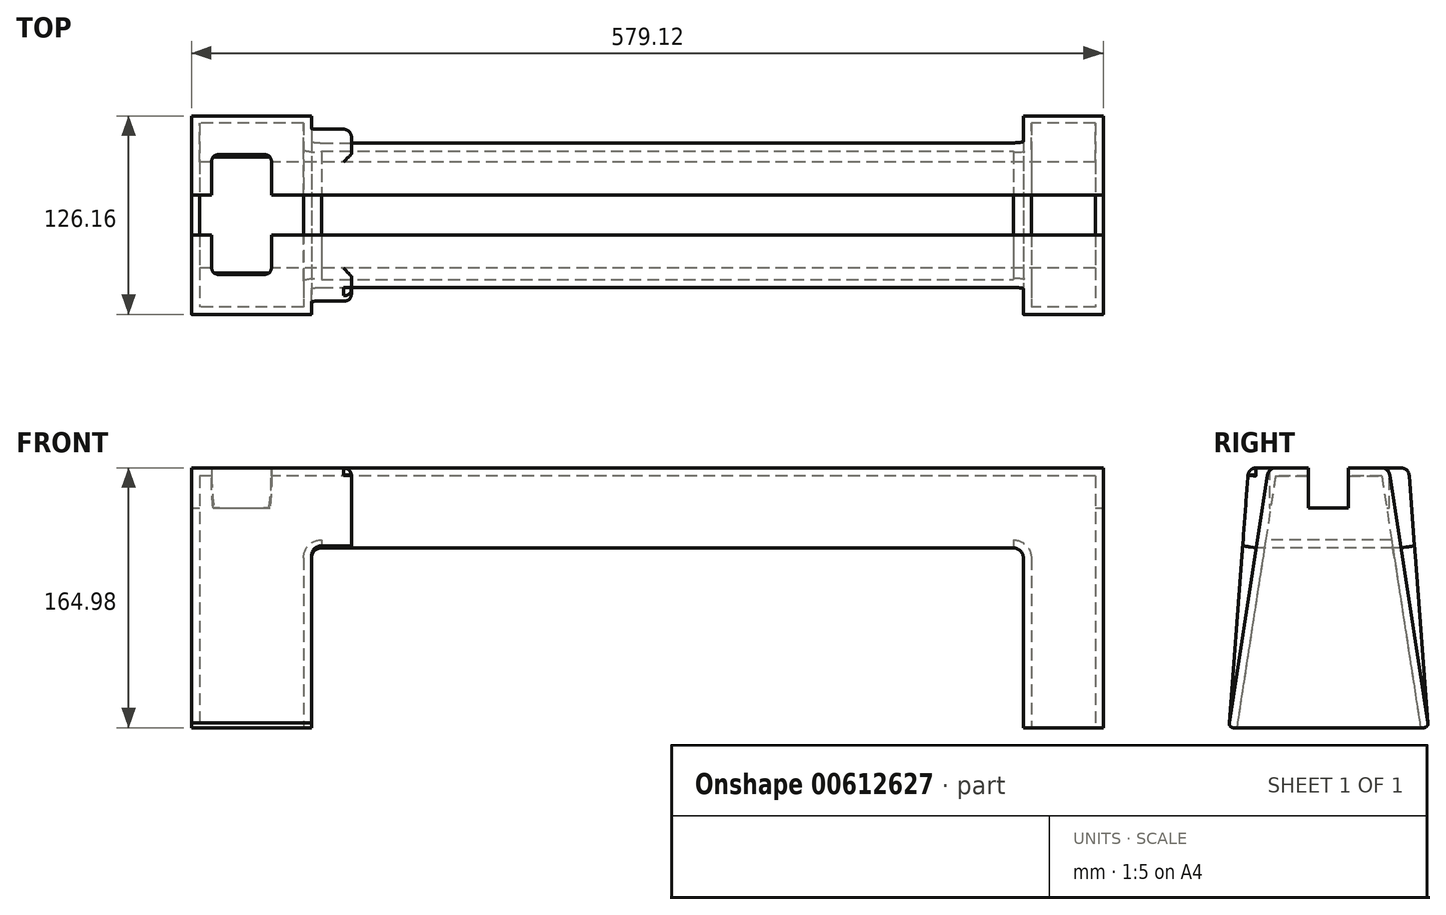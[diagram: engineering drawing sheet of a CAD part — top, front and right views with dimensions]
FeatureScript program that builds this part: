
annotation { "Feature Type Name" : "Feature", "Feature Type Description" : "" }
export const myFeature = defineFeature(function(context is Context, id is Id, definition is map)
    precondition{}
    {
        {
            var Q0;
            Q0=qCreatedBy(makeId("Right.planeOp"),FACE);
            var sketch = newSketch(context, id + "F0", { "sketchPlane" : qUnion([Q0])});
            skLineSegment(sketch, "E0.bottom", {"start": v(60.54, -82.5) * mm, "end": v(-60.54, -82.5) * mm});
            skLineSegment(sketch, "E0.top", {"start": v(38.1, 82.5) * mm, "end": v(-38.1, 82.5) * mm});
            skPoint(sketch, "E0.middle", {"position": v(0, 0) * mm});
            skPoint(sketch, "E1", {"position": v(0, 82.5) * mm});
            skPoint(sketch, "E2", {"position": v(-38.1, 82.5) * mm});
            skPoint(sketch, "E3", {"position": v(38.1, 82.5) * mm});
            skLineSegment(sketch, "E4", {"start": v(-38.1, 82.5) * mm, "end": v(-63.05, -79.57) * mm});
            skLineSegment(sketch, "E5", {"start": v(38.1, 82.5) * mm, "end": v(63.05, -79.57) * mm});
            skPoint(sketch, "E0.right.end.orphan", {"position": v(-63.5, 82.5) * mm});
            skPoint(sketch, "E0.left.end.orphan", {"position": v(63.5, 82.5) * mm});
            skLineSegment(sketch, "E6.filletArc", {"start": v(38.1, 82.5) * mm, "end": v(38.1, 82.5) * mm});
            skPoint(sketch, "E7.visualSharp", {"position": v(63.5, -82.5) * mm});
            skArc(sketch, "E7.filletArc", {"start": v(60.54, -82.5) * mm, "mid": v(62.47, -81.6) * mm, "end": v(63.05, -79.57) * mm});
            skPoint(sketch, "E8.visualSharp", {"position": v(-63.5, -82.5) * mm});
            skArc(sketch, "E8.filletArc", {"start": v(-63.05, -79.57) * mm, "mid": v(-62.47, -81.6) * mm, "end": v(-60.54, -82.5) * mm});
            skLineSegment(sketch, "E9.filletArc", {"start": v(-38.1, 82.5) * mm, "end": v(-38.1, 82.5) * mm});
            skLineSegment(sketch, "E10", {"start": v(-38.1, 82.5) * mm, "end": v(-50.84, 82.5) * mm});
            skLineSegment(sketch, "E11", {"start": v(-50.84, 82.5) * mm, "end": v(-63.05, -79.57) * mm});
            skLineSegment(sketch, "E12.MirrorCS", {"start": v(38.1, 82.5) * mm, "end": v(50.84, 82.5) * mm});
            skLineSegment(sketch, "E13.MirrorCS", {"start": v(50.84, 82.5) * mm, "end": v(63.05, -79.57) * mm});
            skSolve(sketch);
        }
        {
            var Q0;
            Q0=makeQuery(id+"F0.imprint","IMPRINT",FACE,{"disambiguationData":[TD([[makeQuery(id+"F0.imprint","IMPRINT",EDGE,{"derivedFrom":sQuery(id+"F0.wireOp",EDGE,"E0.bottom")}),-1.0]])]});
            extrude(context, id + "F1", {"entities" : qUnion([Q0]), "depth" : 579.12 * mm, "offsetDistance" : 25.4 * mm});
        }
        {
            var Q0;
            Q0=qCreatedBy(makeId("Front.planeOp"),FACE);
            cPlane(context, id + "F2", {"entities" : qUnion([Q0]), "cplaneType" : CPlaneType.OFFSET, "offset" : 25.4 * mm, "width" : 152.4 * mm, "height" : 152.4 * mm});
        }
        {
            var Q0;
            Q0=qCreatedBy(id+"F2.planeOp",FACE);
            var sketch = newSketch(context, id + "F3", { "sketchPlane" : qUnion([Q0])});
            skLineSegment(sketch, "E14.bottom", {"start": v(528.32, -91.26) * mm, "end": v(76.2, -91.26) * mm});
            skLineSegment(sketch, "E14.top", {"start": v(521.97, 31.7) * mm, "end": v(82.55, 31.7) * mm});
            skLineSegment(sketch, "E14.left", {"start": v(528.32, -91.26) * mm, "end": v(528.32, 25.34) * mm});
            skLineSegment(sketch, "E14.right", {"start": v(76.2, -91.26) * mm, "end": v(76.2, 25.34) * mm});
            skPoint(sketch, "E15.visualSharp", {"position": v(76.2, 31.7) * mm});
            skArc(sketch, "E15.filletArc", {"start": v(82.55, 31.7) * mm, "mid": v(78.06, 29.83) * mm, "end": v(76.2, 25.34) * mm});
            skPoint(sketch, "E16.visualSharp", {"position": v(528.32, 31.7) * mm});
            skArc(sketch, "E16.filletArc", {"start": v(528.32, 25.34) * mm, "mid": v(526.46, 29.83) * mm, "end": v(521.97, 31.7) * mm});
            skSolve(sketch);
        }
        {
            var Q0;
            {var subQ0=sQuery(id+"F3.wireOp",EDGE,"E14.top");Q0=makeQuery(id+"F3.imprint","IMPRINT",FACE,{"disambiguationData":[TD([[makeQuery(id+"F3.imprint","IMPRINT",EDGE,{"derivedFrom":subQ0}),1.0]])]});}
            extrude(context, id + "F4", {"entities" : qUnion([Q0]), "operationType" : NewBodyOperationType.REMOVE, "endBound" : BoundingType.THROUGH_ALL, "oppositeDirection" : true, "depth" : 127 * mm, "offsetDistance" : 25.4 * mm, "hasSecondDirection" : true, "secondDirectionOppositeDirection" : false, "secondDirectionDepth" : 76.2 * mm});
        }
        {
            var Q0;
            Q0=makeQuery(id+"F1.opExtrude","SWEPT_FACE",FACE,{"disambiguationData":[OSD([sQuery(id+"F0.wireOp",EDGE,"E0.top")])]});
            var sketch = newSketch(context, id + "F5", { "sketchPlane" : qUnion([Q0])});
            skLineSegment(sketch, "E17", {"start": v(0, 0) * mm, "end": v(0, 12.7) * mm});
            skLineSegment(sketch, "E18", {"start": v(0, 12.7) * mm, "end": v(579.12, 12.7) * mm});
            skLineSegment(sketch, "E19", {"start": v(579.12, 12.7) * mm, "end": v(579.12, -12.7) * mm});
            skLineSegment(sketch, "E20", {"start": v(579.12, -12.7) * mm, "end": v(0, -12.7) * mm});
            skLineSegment(sketch, "E21", {"start": v(0, -12.7) * mm, "end": v(0, 12.7) * mm});
            skSolve(sketch);
        }
        {
            var Q0;
            Q0=makeQuery(id+"F4.boolean.opBoolean","COPY",FACE,{"derivedFrom":makeQuery(id+"F4.opExtrude","SWEPT_FACE",FACE,{"disambiguationData":[OSD([sQuery(id+"F3.wireOp",EDGE,"E14.top")])]})});
            var Q1;
            {var subQ2=sQuery(id+"F0.wireOp",EDGE,"E0.bottom");Q1=makeQuery(id+"F4.boolean.opBoolean","SPLIT",FACE,{"disambiguationData":[TD([makeQuery(id+"F4.opExtrude","SWEPT_FACE",FACE,{"disambiguationData":[OSD([sQuery(id+"F3.wireOp",EDGE,"E14.right")])]})])],"derivedFrom":makeQuery(id+"F1.opExtrude","SWEPT_FACE",FACE,{"disambiguationData":[OSD([subQ2])]})});}
            var Q2;
            {var subQ2=sQuery(id+"F0.wireOp",EDGE,"E0.bottom");Q2=makeQuery(id+"F4.boolean.opBoolean","SPLIT",FACE,{"disambiguationData":[TD([makeQuery(id+"F4.opExtrude","SWEPT_FACE",FACE,{"disambiguationData":[OSD([sQuery(id+"F3.wireOp",EDGE,"E14.left")])]})])],"derivedFrom":makeQuery(id+"F1.opExtrude","SWEPT_FACE",FACE,{"disambiguationData":[OSD([subQ2])]})});}
            shell(context, id + "F6", {"entities" : qUnion([Q0, Q1, Q2]), "thickness" : 5.08 * mm});
        }
        {
            var Q0;
            {var subQ0=sQuery(id+"F5.wireOp",EDGE,"E18");Q0=makeQuery(id+"F5.imprint","IMPRINT",FACE,{"disambiguationData":[TD([[makeQuery(id+"F5.imprint","IMPRINT",EDGE,{"derivedFrom":subQ0}),-1.0]])]});}
            extrude(context, id + "F7", {"entities" : qUnion([Q0]), "operationType" : NewBodyOperationType.REMOVE, "oppositeDirection" : true, "depth" : 25.4 * mm, "offsetDistance" : 25.4 * mm});
        }
        {
            var Q0;
            Q0=makeQuery(id+"F0.imprint","IMPRINT",FACE,{"disambiguationData":[TD([[makeQuery(id+"F0.imprint","IMPRINT",EDGE,{"derivedFrom":sQuery(id+"F0.wireOp",EDGE,"E4")}),-1.0]])]});
            var Q1;
            Q1=makeQuery(id+"F0.imprint","IMPRINT",FACE,{"disambiguationData":[TD([[makeQuery(id+"F0.imprint","IMPRINT",EDGE,{"derivedFrom":sQuery(id+"F0.wireOp",EDGE,"E5")}),1.0]])]});
            extrude(context, id + "F8", {"entities" : qUnion([Q0, Q1]), "operationType" : NewBodyOperationType.ADD, "depth" : 101.6 * mm, "offsetDistance" : 25.4 * mm});
        }
        {
            var Q0;
            Q0=makeQuery(id+"F8.opExtrude","SWEPT_FACE",FACE,{"disambiguationData":[OSD([sQuery(id+"F0.wireOp",EDGE,"E5")])]});
            extrude(context, id + "F9", {"entities" : qUnion([Q0]), "operationType" : NewBodyOperationType.REMOVE, "oppositeDirection" : true, "depth" : 25.4 * mm, "offsetDistance" : 25.4 * mm});
        }
        {
            var Q0;
            Q0=makeQuery(id+"F8.opExtrude","SWEPT_FACE",FACE,{"disambiguationData":[OSD([sQuery(id+"F0.wireOp",EDGE,"E4")])]});
            extrude(context, id + "F10", {"entities" : qUnion([Q0]), "operationType" : NewBodyOperationType.REMOVE, "oppositeDirection" : true, "depth" : 25.4 * mm, "offsetDistance" : 25.4 * mm});
        }
        {
            var Q0;
            Q0=makeQuery(id+"F8.opExtrude","SWEPT_EDGE",EDGE,{"disambiguationData":[OSD([sQuery(id+"F0.wireOp",EDGE,"E12.MirrorCS"),sQuery(id+"F0.wireOp",EDGE,"E13.MirrorCS")])]});
            var Q1;
            Q1=makeQuery(id+"F8.opExtrude","CAP_EDGE",EDGE,{"disambiguationData":[OSD([sQuery(id+"F0.wireOp",EDGE,"E13.MirrorCS")])],"isStart":false});
            var Q2;
            Q2=makeQuery(id+"F8.opExtrude","CAP_EDGE",EDGE,{"disambiguationData":[OSD([sQuery(id+"F0.wireOp",EDGE,"E12.MirrorCS")])],"isStart":false});
            var Q3;
            Q3=makeQuery(id+"F1.opExtrude","SWEPT_EDGE",EDGE,{"disambiguationData":[OSD([sQuery(id+"F0.wireOp",EDGE,"E0.top"),sQuery(id+"F0.wireOp",EDGE,"E5"),sQuery(id+"F0.wireOp",EDGE,"E12.MirrorCS")])]});
            var Q4;
            Q4=makeQuery(id+"F1.opExtrude","SWEPT_EDGE",EDGE,{"disambiguationData":[OSD([sQuery(id+"F0.wireOp",EDGE,"E0.top"),sQuery(id+"F0.wireOp",EDGE,"E4"),sQuery(id+"F0.wireOp",EDGE,"E10")])]});
            var Q5;
            Q5=makeQuery(id+"F8.opExtrude","CAP_EDGE",EDGE,{"disambiguationData":[OSD([sQuery(id+"F0.wireOp",EDGE,"E10")])],"isStart":false});
            var Q6;
            Q6=makeQuery(id+"F8.opExtrude","SWEPT_EDGE",EDGE,{"disambiguationData":[OSD([sQuery(id+"F0.wireOp",EDGE,"E10"),sQuery(id+"F0.wireOp",EDGE,"E11")])]});
            fillet(context, id + "F11", {"entities" : qUnion([Q0, Q1, Q2, Q3, Q4, Q5, Q6]), "radius" : 5.08 * mm, "tangentPropagation" : true, "allowEdgeOverflow" : false});
        }
        {
            var Q0;
            {var subQ2=sQuery(id+"F0.wireOp",EDGE,"E5");var subQ4=sQuery(id+"F0.wireOp",EDGE,"E0.top");Q0=makeQuery(id+"F8.boolean.opBoolean","MERGE",FACE,{"derivedFrom":[makeQuery(id+"F7.boolean.opBoolean","SPLIT",FACE,{"disambiguationData":[TD([makeQuery(id+"F1.opExtrude","SWEPT_FACE",FACE,{"disambiguationData":[OSD([subQ2])]})])],"derivedFrom":makeQuery(id+"F1.opExtrude","SWEPT_FACE",FACE,{"disambiguationData":[OSD([subQ4])]})}),makeQuery(id+"F8.opExtrude","SWEPT_FACE",FACE,{"disambiguationData":[OSD([sQuery(id+"F0.wireOp",EDGE,"E12.MirrorCS")])]})]});}
            var sketch = newSketch(context, id + "F12", { "sketchPlane" : qUnion([Q0])});
            skLineSegment(sketch, "E22.bottom", {"start": v(12.7, 38.5) * mm, "end": v(50.8, 38.5) * mm});
            skLineSegment(sketch, "E22.top", {"start": v(12.7, -37.7) * mm, "end": v(50.8, -37.7) * mm});
            skLineSegment(sketch, "E22.left", {"start": v(12.7, 38.5) * mm, "end": v(12.7, -37.7) * mm});
            skLineSegment(sketch, "E22.right", {"start": v(50.8, 38.5) * mm, "end": v(50.8, -37.7) * mm});
            skSolve(sketch);
        }
        {
            var Q0;
            {var subQ0=sQuery(id+"F12.wireOp",EDGE,"E22.top");Q0=makeQuery(id+"F12.imprint","IMPRINT",FACE,{"disambiguationData":[TD([[makeQuery(id+"F12.imprint","IMPRINT",EDGE,{"derivedFrom":subQ0}),1.0]])]});}
            var Q1;
            {var subQ0=sQuery(id+"F12.wireOp",EDGE,"E22.bottom");Q1=makeQuery(id+"F12.imprint","IMPRINT",FACE,{"disambiguationData":[TD([[makeQuery(id+"F12.imprint","IMPRINT",EDGE,{"derivedFrom":subQ0}),-1.0]])]});}
            extrude(context, id + "F13", {"entities" : qUnion([Q0, Q1]), "operationType" : NewBodyOperationType.REMOVE, "oppositeDirection" : true, "depth" : 25.4 * mm, "offsetDistance" : 25.4 * mm});
        }
        {
            var Q0;
            Q0=makeQuery(id+"F13.boolean.opBoolean","COPY",EDGE,{"derivedFrom":makeQuery(id+"F13.opExtrude","SWEPT_EDGE",EDGE,{"disambiguationData":[OSD([sQuery(id+"F12.wireOp",EDGE,"E22.bottom"),sQuery(id+"F12.wireOp",EDGE,"E22.right")])]})});
            var Q1;
            Q1=makeQuery(id+"F8.opExtrude","CAP_EDGE",EDGE,{"disambiguationData":[OSD([sQuery(id+"F0.wireOp",EDGE,"E11")])],"isStart":false});
            var Q2;
            Q2=makeQuery(id+"F13.boolean.opBoolean","COPY",EDGE,{"derivedFrom":makeQuery(id+"F13.opExtrude","SWEPT_EDGE",EDGE,{"disambiguationData":[OSD([sQuery(id+"F12.wireOp",EDGE,"E22.bottom"),sQuery(id+"F12.wireOp",EDGE,"E22.left")])]})});
            var Q3;
            Q3=makeQuery(id+"F13.boolean.opBoolean","COPY",EDGE,{"derivedFrom":makeQuery(id+"F13.opExtrude","SWEPT_EDGE",EDGE,{"disambiguationData":[OSD([sQuery(id+"F12.wireOp",EDGE,"E22.top"),sQuery(id+"F12.wireOp",EDGE,"E22.left")])]})});
            var Q4;
            Q4=makeQuery(id+"F13.boolean.opBoolean","COPY",EDGE,{"derivedFrom":makeQuery(id+"F13.opExtrude","SWEPT_EDGE",EDGE,{"disambiguationData":[OSD([sQuery(id+"F12.wireOp",EDGE,"E22.top"),sQuery(id+"F12.wireOp",EDGE,"E22.right")])]})});
            fillet(context, id + "F14", {"entities" : qUnion([Q0, Q1, Q2, Q3, Q4]), "radius" : 5.08 * mm, "tangentPropagation" : true, "rho" : 0.5, "crossSection" : FilletCrossSection.CONIC, "allowEdgeOverflow" : false});
        }
    });
